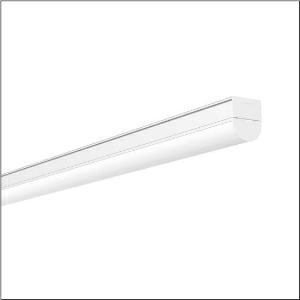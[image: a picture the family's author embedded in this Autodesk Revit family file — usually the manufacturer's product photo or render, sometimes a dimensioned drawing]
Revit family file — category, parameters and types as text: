
# Revit family: ecopack_r__31_51lj12mdm20a_29c1
name_source: partatom
category: Lighting Fixtures
units: mm (PartAtom-declared; Revit-internal decimal feet)

## family parameters
Cut with Voids When Loaded = No
Host = Face
Light Source = No
Part Type = Normal
Room Calculation Point = No
Round Connector Dimension = Use Diameter
Shared = No

## types (1)
- --- (1 x LED, 2510 lm, 20 W, 5000K)
    Apparent Load = 20 VA
    CIE Flux Codes = 41 71 90 93 100
    Color Rendering = 80
    Color Temperature = 5000K
    Default Elevation = 1800 mm
    Description = Ecopack® 31, diffuser luminaire, primary optical cover: cover, of PC, frosted, light emission: direct distribution, primary light characteristic: symmetric, installation type: surface-mounted, LED, rated luminous flux: 2.600lm, luminous efficacy: 130lm/W, light colour: 830/840/850, colour temperature: 3000/4000/5000K, control gear: ECG, with terminal, 3-pole, mains connection: 220..240V, AC, 50/60Hz, rated input power: 20W, housing, of aluminium, traffic white (RAL 9016), length: 600mm, width: 56mm, height: 68mm, end cap, of PC, white, protection rating (complete): IP20, insulation class (complete): insulation class I (protective earthing), certification: CE, impact resistance: IK06, permissible operating ambient temperature: -20..+40°C, packaging unit: 1 piece
    Height = 68 mm
    Lamp = 1 x LED
    Lamp Light Flux = 2510 lm
    Lamp Power = 20 W
    Lamp count = 1
    Length = 600 mm
    Luminous efficacy = 126 lm/W
    Manufacturer = Siteco
    ModVariant = No
    Model = 51LJ12MDM20A
    Mounting Place = Ceiling
    Mounting Type = Surface mounted
    Number of Poles = 1
    OnlyDefault = Yes
    Power Factor = 1
    Product Name = Ecopack® 31
    Product group = diffuser luminaire
    ProductGroupID = 303
    Protection Class = Protection class I
    Protection Degree = IP 20
    RLX_Detail_Level = 1
    RLX_Emergency_Light_Flux = 0 lm
    RLX_Emergency_Type = 0
    RLX_Emergency_Type_DB = No
    RlxData = <blob elided: 25673 chars, md5=d804a923>
    Socket = socket
    Standby Power = 0 W
    System Light Flux = 2510 lm
    System Power = 20 W
    Type Comments = individual setting: colour temperature 5000K, luminous flux: 100 % | (ON | ON)
    Type Image = l_1007030.jpg
    URL = http://relux.com
    VarID = @adj_107131
    Voltage = 0 V
    Weight = 0.00 kg
    Width = 56 mm

## geometry (parser evidence)
native form markers: Blend x4, Sweep x12
no freeform markers — native parametric forms only
